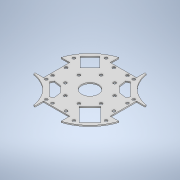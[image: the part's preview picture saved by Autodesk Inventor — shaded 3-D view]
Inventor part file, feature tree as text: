
AUTODESK INVENTOR PART (.ipt)
format: ipt  version: 2020 (Build 240168000, 168)  size: 281,088 bytes
history: native  units: mm
features: extrude x3, sketch x3, other x1, projected_geometry x1
ambient origin geometry x8: Origin, YZ Plane, XZ Plane, XY Plane, X Axis, Y Axis, Z Axis, Center Point
bodies: Body1 (feature_tree)
feature tree (8):
  other  "Твердое тело1"
  extrude  "Выдавливание1"  Depth=2.66mm TaperAngle=0.0deg
  extrude  "Выдавливание2"  Depth=6.6mm
  extrude  "Выдавливание3"  Depth=2.66mm TaperAngle=0.0deg
  sketch  "Эскиз3"
  sketch  "Эскиз5"
  projected_geometry  "Спроецированная петля1"
  sketch  "Эскиз6"
